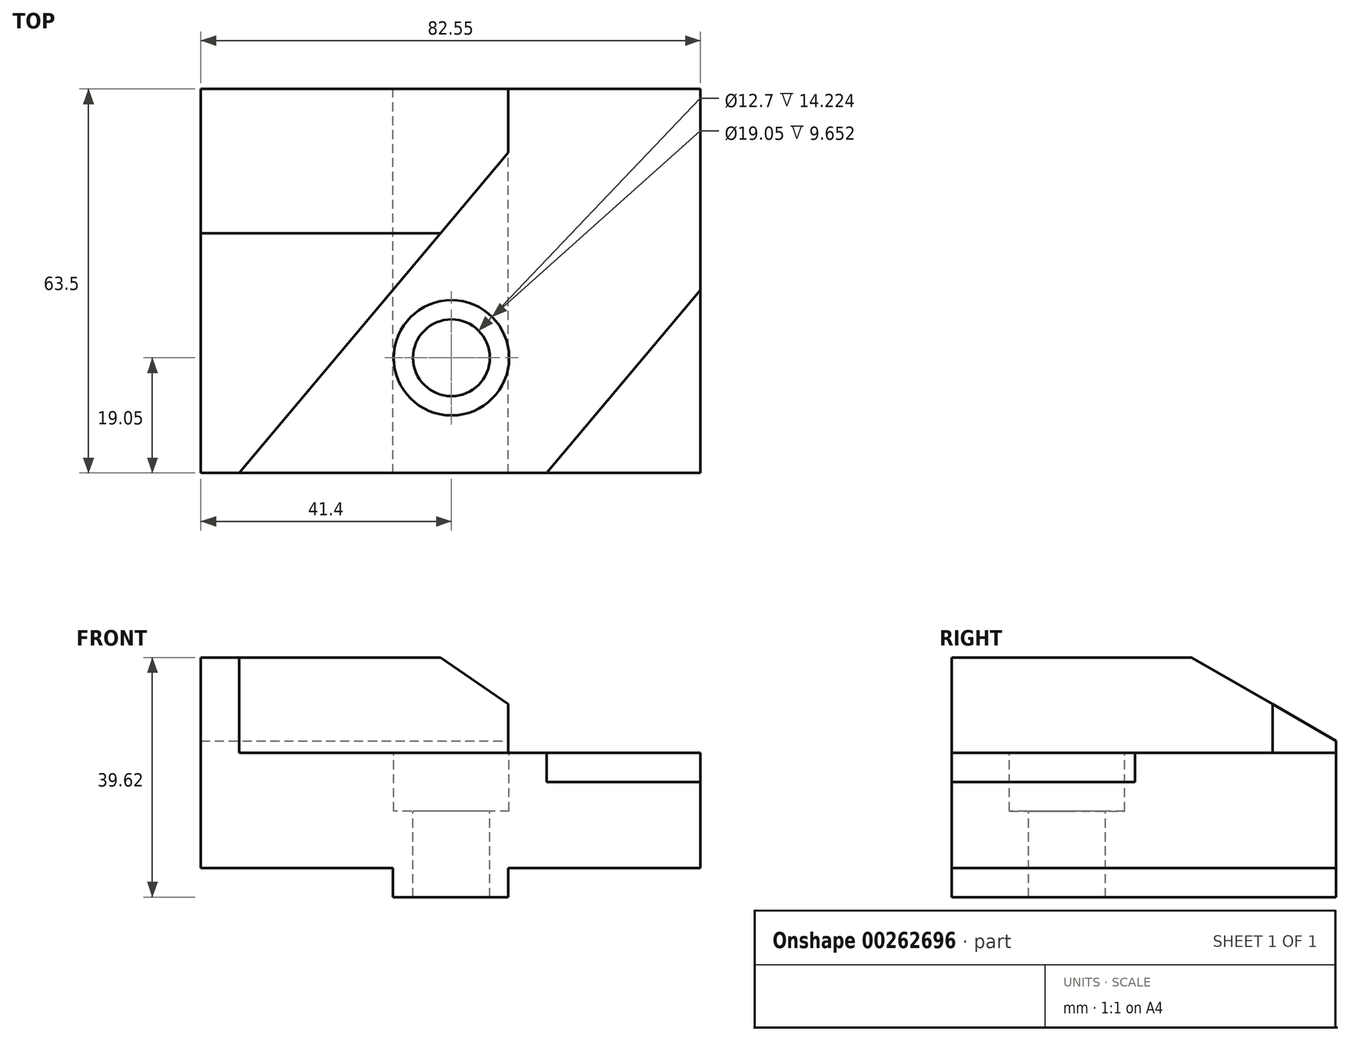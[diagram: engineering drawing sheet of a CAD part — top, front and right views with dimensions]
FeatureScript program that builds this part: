
annotation { "Feature Type Name" : "Feature", "Feature Type Description" : "" }
export const myFeature = defineFeature(function(context is Context, id is Id, definition is map)
    precondition{}
    {
        {
            var Q0;
            Q0=qCreatedBy(makeId("Front.planeOp"),FACE);
            var sketch = newSketch(context, id + "F0", { "sketchPlane" : qUnion([Q0])});
            skLineSegment(sketch, "E0.bottom", {"start": v(-3.42, 26.83) * mm, "end": v(-54.22, 26.83) * mm});
            skLineSegment(sketch, "E0.top", {"start": v(-3.42, -12.8) * mm, "end": v(-22.47, -12.8) * mm});
            skLineSegment(sketch, "E0.left", {"start": v(28.33, 11.08) * mm, "end": v(28.33, -7.97) * mm});
            skLineSegment(sketch, "E0.right", {"start": v(-54.22, 26.83) * mm, "end": v(-54.22, -7.97) * mm});
            skLineSegment(sketch, "E1.top", {"start": v(-54.22, -7.97) * mm, "end": v(-22.47, -7.97) * mm});
            skLineSegment(sketch, "E1.right", {"start": v(-22.47, -12.8) * mm, "end": v(-22.47, -7.97) * mm});
            skLineSegment(sketch, "E2.top", {"start": v(28.33, -7.97) * mm, "end": v(-3.42, -7.97) * mm});
            skLineSegment(sketch, "E2.right", {"start": v(-3.42, -12.8) * mm, "end": v(-3.42, -7.97) * mm});
            skLineSegment(sketch, "E3.bottom", {"start": v(28.33, 11.08) * mm, "end": v(-3.42, 11.08) * mm});
            skLineSegment(sketch, "E3.right", {"start": v(-3.42, 11.08) * mm, "end": v(-3.42, 26.83) * mm});
            skSolve(sketch);
        }
        {
            var Q0;
            Q0 = qSketchRegion(id + "F0", true);
            extrude(context, id + "F1", {"entities" : qUnion([Q0]), "depth" : 63.5 * mm});
        }
        {
            var Q0;
            Q0=makeQuery(id+"F1.opExtrude","SWEPT_FACE",FACE,{"disambiguationData":[OSD([sQuery(id+"F0.wireOp",EDGE,"E0.bottom")])]});
            var sketch = newSketch(context, id + "F2", { "sketchPlane" : qUnion([Q0])});
            skLineSegment(sketch, "E4", {"start": v(-47.87, -63.5) * mm, "end": v(-3.42, -10.53) * mm});
            skLineSegment(sketch, "E5", {"start": v(-3.42, -10.53) * mm, "end": v(-3.42, -63.5) * mm});
            skLineSegment(sketch, "E6", {"start": v(-3.42, -63.5) * mm, "end": v(-47.87, -63.5) * mm});
            skSolve(sketch);
        }
        {
            var Q0;
            Q0 = qSketchRegion(id + "F2", true);
            extrude(context, id + "F3", {"entities" : qUnion([Q0]), "operationType" : NewBodyOperationType.REMOVE, "oppositeDirection" : true, "depth" : 15.75 * mm});
        }
        {
            var Q0;
            Q0=makeQuery(id+"F3.boolean.opBoolean","MERGE",FACE,{"derivedFrom":[makeQuery(id+"F1.opExtrude","SWEPT_FACE",FACE,{"disambiguationData":[OSD([sQuery(id+"F0.wireOp",EDGE,"E3.bottom")])]}),makeQuery(id+"F3.opExtrude","CAP_FACE",FACE,{"disambiguationData":[OSD([sQuery(id+"F2.wireOp",EDGE,"E4"),sQuery(id+"F2.wireOp",EDGE,"E5"),sQuery(id+"F2.wireOp",EDGE,"E6")])],"isStart":false})]});
            var sketch = newSketch(context, id + "F4", { "sketchPlane" : qUnion([Q0])});
            skLineSegment(sketch, "E7.bottom", {"start": v(28.33, -63.5) * mm, "end": v(2.93, -63.5) * mm});
            skLineSegment(sketch, "E7.left", {"start": v(28.33, -63.5) * mm, "end": v(28.33, -33.23) * mm});
            skLineSegment(sketch, "E8", {"start": v(2.93, -63.5) * mm, "end": v(28.33, -33.23) * mm});
            skSolve(sketch);
        }
        {
            var Q0;
            Q0 = qSketchRegion(id + "F4", true);
            extrude(context, id + "F5", {"entities" : qUnion([Q0]), "operationType" : NewBodyOperationType.REMOVE, "oppositeDirection" : true, "depth" : 4.83 * mm});
        }
        {
            var Q0;
            Q0=makeQuery(id+"F1.opExtrude","SWEPT_FACE",FACE,{"disambiguationData":[OSD([sQuery(id+"F0.wireOp",EDGE,"E3.right")])]});
            var sketch = newSketch(context, id + "F6", { "sketchPlane" : qUnion([Q0])});
            skLineSegment(sketch, "E9.top", {"start": v(0, 26.83) * mm, "end": v(-23.88, 26.83) * mm});
            skLineSegment(sketch, "E9.left", {"start": v(0, 13.05) * mm, "end": v(0, 26.83) * mm});
            skLineSegment(sketch, "E10", {"start": v(-23.88, 26.83) * mm, "end": v(0, 13.05) * mm});
            skSolve(sketch);
        }
        {
            var Q0;
            Q0 = qSketchRegion(id + "F6", true);
            extrude(context, id + "F7", {"entities" : qUnion([Q0]), "operationType" : NewBodyOperationType.REMOVE, "oppositeDirection" : true, "depth" : 55.12 * mm});
        }
        {
            var Q0;
            Q0=makeQuery(id+"F3.boolean.opBoolean","MERGE",FACE,{"derivedFrom":[makeQuery(id+"F1.opExtrude","SWEPT_FACE",FACE,{"disambiguationData":[OSD([sQuery(id+"F0.wireOp",EDGE,"E3.bottom")])]}),makeQuery(id+"F3.opExtrude","CAP_FACE",FACE,{"disambiguationData":[OSD([sQuery(id+"F2.wireOp",EDGE,"E4"),sQuery(id+"F2.wireOp",EDGE,"E5"),sQuery(id+"F2.wireOp",EDGE,"E6")])],"isStart":false})]});
            var sketch = newSketch(context, id + "F8", { "sketchPlane" : qUnion([Q0])});
            skCircle(sketch, "E11", {"center": v(-12.82, -44.45) * mm, "radius": 7.03 * mm});
            skSolve(sketch);
        }
        {
            var Q0;
            Q0=sQuery(id+"F8.wireOp",VERTEX,"E11.center");
            var Q1;
            Q1=makeQuery(id+"F1.opExtrude","SWEPT_BODY",BODY,{"disambiguationData":[OSD([sQuery(id+"F0.wireOp",EDGE,"E0.bottom"),sQuery(id+"F0.wireOp",EDGE,"E0.top"),sQuery(id+"F0.wireOp",EDGE,"E0.left"),sQuery(id+"F0.wireOp",EDGE,"E0.right"),sQuery(id+"F0.wireOp",EDGE,"E1.top"),sQuery(id+"F0.wireOp",EDGE,"E1.right"),sQuery(id+"F0.wireOp",EDGE,"E2.top"),sQuery(id+"F0.wireOp",EDGE,"E2.right"),sQuery(id+"F0.wireOp",EDGE,"E3.bottom"),sQuery(id+"F0.wireOp",EDGE,"E3.right")])]});
            hole(context, id + "F9", {"style" : HoleStyle.C_BORE, "endStyle" : HoleEndStyle.THROUGH, "holeDiameter" : 12.7 * mm, "cBoreDiameter" : 19.05 * mm, "cBoreDepth" : 9.65 * mm, "tappedDepth" : 12.7 * mm, "tapClearance" : 3, "startFromSketch" : true, "locations" : qUnion([Q0]), "scope" : qUnion([Q1])});
        }
    });
